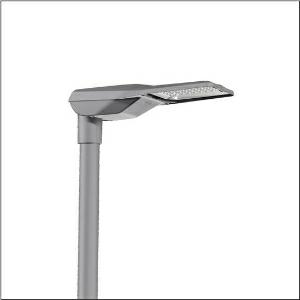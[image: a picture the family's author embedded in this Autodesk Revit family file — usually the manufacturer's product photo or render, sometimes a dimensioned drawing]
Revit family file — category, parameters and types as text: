
# Revit family: streetlight_sl_21_iq_mini___st1_5a_5xe2p31d08hb_3c75
name_source: partatom
category: Lighting Fixtures
units: mm (PartAtom-declared; Revit-internal decimal feet)

## family parameters
Cut with Voids When Loaded = No
Host = Face
Light Source = No
Part Type = Normal
Room Calculation Point = No
Round Connector Dimension = Use Diameter
Shared = No

## types (1)
- --- (1 x LED, 9290 lm, 70.9 W, 3000K)
    Apparent Load = 71 VA
    CIE Flux Codes = 22 53 95 100 100
    Color Rendering = 70
    Color Temperature = 3000K
    Default Elevation = 1800 mm
    Description = Streetlight SL 21 iQ mini, mast luminaire, primary light control with lens, of PMMA, primary optical cover: cover, of toughened safety glass, transparent, light distribution: ST1.5a, light emission: direct distribution, primary light characteristic: asymmetric, installation type: post-top, side-entry, LED, High Power LED, rated luminous flux: 9.290lm, luminous efficacy: 131lm/W, light colour: 730, colour temperature: 3000K, control gear: iQ-Comfort, control: Auto-Match, Temp-Guard, Lumen-Switch, Night-Set, Smart-Wire, Light-Fading, Desk-Remote (wireless, voltage-free reading and setting of iQ features in the workshop via application-optimized NFC function/RFID function), optimised constant luminous flux control (CLO 2.0), pre-setting: linear dimming characteristic, mains connection: 220..240V, AC, 50/60Hz, start of lifetime: 71W, end of service life: 75W, reduction: 31W, luminaire housing, of diecast aluminium, powder-coated, SITECO metallic grey (DB 702S), corrosivity category C5 high according to DIN EN ISO 12944, please order mast flange separately, inclination adjustable: 0°, 5°, 10°, 15°, sealing non-destructively replaceable, multi-level sealing system, length: 628mm, width: 235mm, height: 110mm, mast flange for spigot size: 42mm (side-entry): 5XC10008XM4, 60/48mm (side-entry/post-top): 5XC10108XM2, 76/60mm (side-entry/post-top): 5XC10108XM1, mounting height: 4..8m, protection rating (complete): IP66, insulation class (complete): insulation class II (safety insulation), certification: CE, ENEC, ENEC+, VDE, impact resistance: IK10, permissible operating ambient temperature for outdoor applications: -40..+50°C, standard-compliant lighting for roads and squares, packaging unit: 1 piece

Light Distribution: ST1.5a
    Height = 110 mm
    Lamp = 1 x LED
    Lamp Light Flux = 9290 lm
    Lamp Power = 70.9 W
    Lamp count = 1
    Length = 625 mm
    Luminous efficacy = 131 lm/W
    Manufacturer = Siteco
    ModVariant = No
    Model = 5XE2P31D08HB
    Number of Poles = 1
    OnlyDefault = Yes
    Power Factor = 1
    Product Name = Streetlight SL 21 iQ mini | ST1.5a
    Product group = mast luminaire | pylon top
    ProductGroupID = 6100
    Protection Class = Protection class II
    Protection Degree = IP 66
    RLX_Detail_Level = 1
    RLX_Emergency_Light_Flux = 0 lm
    RLX_Emergency_Type = 0
    RLX_Emergency_Type_DB = No
    RlxData = <blob elided: 29877 chars, md5=41d98385>
    Socket = socket
    Standby Power = 0 W
    System Light Flux = 9290 lm
    System Power = 71 W
    Type Comments = factory setting: luminous flux: 100 % | dim-lin: 254 | 711 mA
    Type Image = l_1003519.jpg
    URL = http://relux.com
    VarID = @adj_156577
    Voltage = 0 V
    Weight = 0.00 kg
    Width = 234 mm

## geometry (parser evidence)
native form markers: Blend x4, Sweep x11
no freeform markers — native parametric forms only
